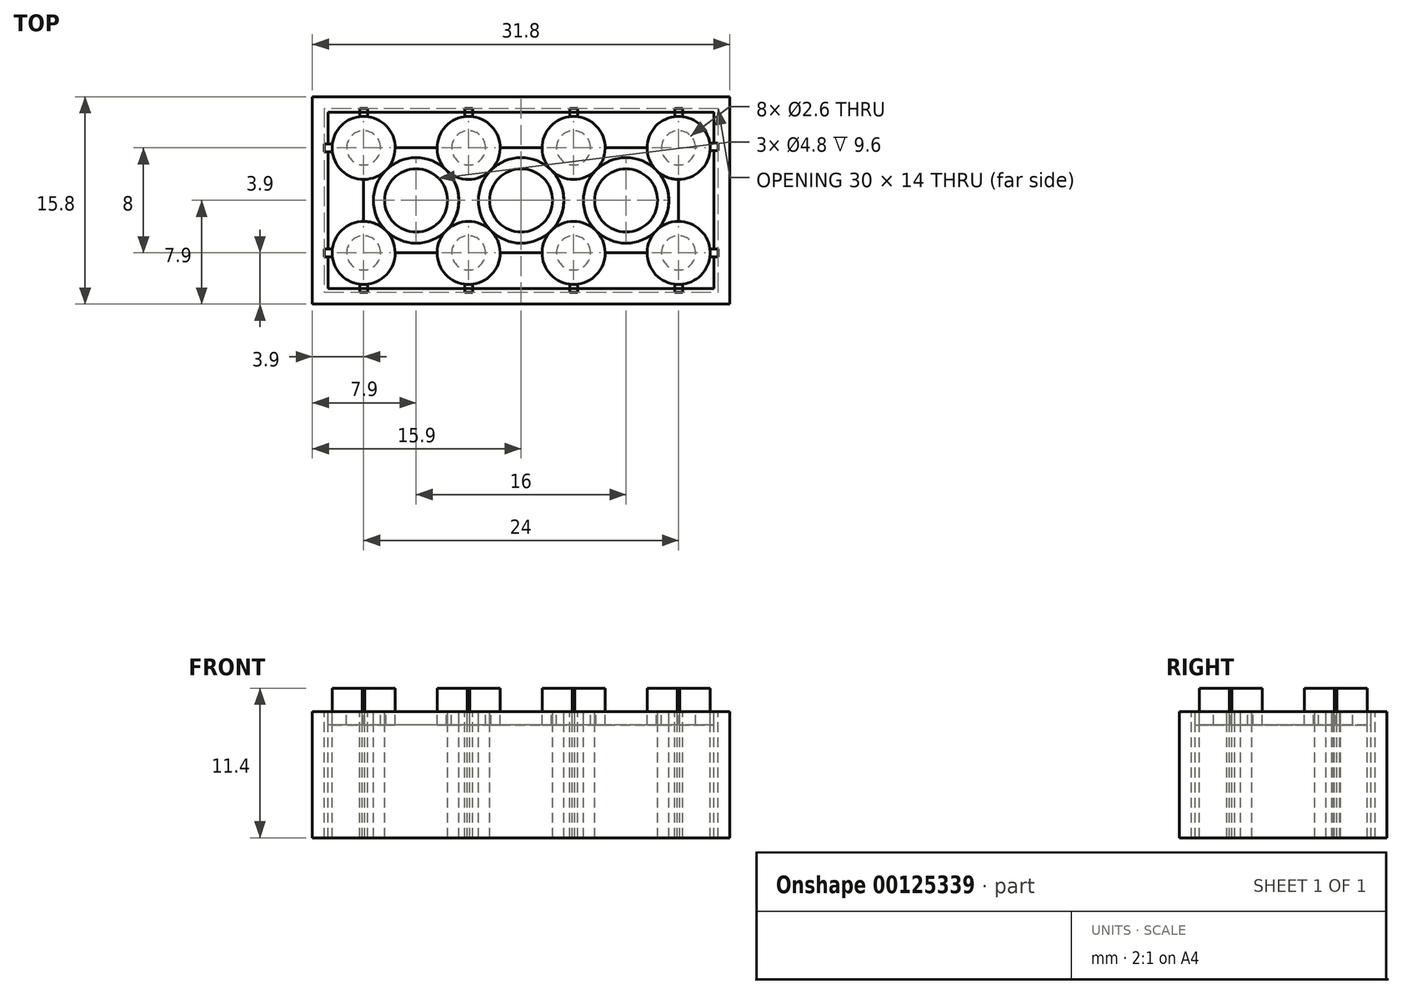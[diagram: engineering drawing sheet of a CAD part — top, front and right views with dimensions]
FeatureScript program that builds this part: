
annotation { "Feature Type Name" : "Feature", "Feature Type Description" : "" }
export const myFeature = defineFeature(function(context is Context, id is Id, definition is map)
    precondition{}
    {
        {
            var Q0;
            Q0=qCreatedBy(makeId("Top.planeOp"),FACE);
            var sketch = newSketch(context, id + "F0", { "sketchPlane" : qUnion([Q0])});
            skLineSegment(sketch, "E0.bottom", {"start": v(-15.9, -7.9) * mm, "end": v(15.9, -7.9) * mm});
            skLineSegment(sketch, "E0.top", {"start": v(-15.9, 7.9) * mm, "end": v(15.9, 7.9) * mm});
            skLineSegment(sketch, "E0.left", {"start": v(-15.9, -7.9) * mm, "end": v(-15.9, 7.9) * mm});
            skLineSegment(sketch, "E0.right", {"start": v(15.9, -7.9) * mm, "end": v(15.9, 7.9) * mm});
            skPoint(sketch, "E0.middle", {"position": v(0, 0) * mm});
            skCircle(sketch, "E1", {"center": v(0, 0) * mm, "radius": 3.26 * mm});
            skCircle(sketch, "E2", {"center": v(0, 0) * mm, "radius": 2.4 * mm});
            skLineSegment(sketch, "E3.bottom", {"start": v(14.7, -6.7) * mm, "end": v(-14.7, -6.7) * mm});
            skLineSegment(sketch, "E3.top", {"start": v(14.7, 6.7) * mm, "end": v(-14.7, 6.7) * mm});
            skLineSegment(sketch, "E3.left", {"start": v(14.7, -6.7) * mm, "end": v(14.7, 6.7) * mm});
            skLineSegment(sketch, "E3.right", {"start": v(-14.7, -6.7) * mm, "end": v(-14.7, 6.7) * mm});
            skPoint(sketch, "E4.endSnap0", {"position": v(-14.7, 0) * mm});
            skPoint(sketch, "E5.endSnap0", {"position": v(14.7, 0) * mm});
            skCircle(sketch, "E6", {"center": v(8, 0) * mm, "radius": 3.26 * mm});
            skCircle(sketch, "E7", {"center": v(8, 0) * mm, "radius": 2.4 * mm});
            skCircle(sketch, "E8", {"center": v(-8, 0) * mm, "radius": 3.26 * mm});
            skCircle(sketch, "E9", {"center": v(-8, 0) * mm, "radius": 2.4 * mm});
            skLineSegment(sketch, "E10", {"start": v(-14.7, 0) * mm, "end": v(14.7, 0) * mm});
            skLineSegment(sketch, "E11.bottom", {"start": v(-4, 4) * mm, "end": v(4, 4) * mm});
            skLineSegment(sketch, "E11.top", {"start": v(-4, -4) * mm, "end": v(4, -4) * mm});
            skLineSegment(sketch, "E11.left", {"start": v(-4, 4) * mm, "end": v(-4, -4) * mm});
            skLineSegment(sketch, "E11.right", {"start": v(4, 4) * mm, "end": v(4, -4) * mm});
            skCircle(sketch, "E12", {"center": v(-4, 4) * mm, "radius": 2.4 * mm});
            skCircle(sketch, "E13", {"center": v(4, 4) * mm, "radius": 2.4 * mm});
            skCircle(sketch, "E14", {"center": v(4, -4) * mm, "radius": 2.4 * mm});
            skCircle(sketch, "E15", {"center": v(-4, -4) * mm, "radius": 2.4 * mm});
            skCircle(sketch, "E16", {"center": v(-4, 4) * mm, "radius": 1.3 * mm});
            skCircle(sketch, "E17", {"center": v(4, 4) * mm, "radius": 1.3 * mm});
            skCircle(sketch, "E18", {"center": v(-4, -4) * mm, "radius": 1.3 * mm});
            skCircle(sketch, "E19", {"center": v(4, -4) * mm, "radius": 1.3 * mm});
            skLineSegment(sketch, "E20", {"start": v(-8, 0) * mm, "end": v(0, 0) * mm});
            skLineSegment(sketch, "E21", {"start": v(0, 0) * mm, "end": v(8, 0) * mm});
            skLineSegment(sketch, "E22.bottom", {"start": v(-4, 4) * mm, "end": v(-12, 4) * mm});
            skLineSegment(sketch, "E22.top", {"start": v(-4, -4) * mm, "end": v(-12, -4) * mm});
            skLineSegment(sketch, "E22.right", {"start": v(-12, 4) * mm, "end": v(-12, -4) * mm});
            skLineSegment(sketch, "E23.bottom", {"start": v(4, 4) * mm, "end": v(12, 4) * mm});
            skLineSegment(sketch, "E23.top", {"start": v(4, -4) * mm, "end": v(12, -4) * mm});
            skLineSegment(sketch, "E23.right", {"start": v(12, 4) * mm, "end": v(12, -4) * mm});
            skCircle(sketch, "E24", {"center": v(-12, 4) * mm, "radius": 2.4 * mm});
            skCircle(sketch, "E25", {"center": v(-12, -4) * mm, "radius": 2.4 * mm});
            skCircle(sketch, "E26", {"center": v(12, -4) * mm, "radius": 2.4 * mm});
            skCircle(sketch, "E27", {"center": v(12, 4) * mm, "radius": 2.4 * mm});
            skCircle(sketch, "E28", {"center": v(-12, 4) * mm, "radius": 1.3 * mm});
            skCircle(sketch, "E29", {"center": v(-12, -4) * mm, "radius": 1.3 * mm});
            skCircle(sketch, "E30", {"center": v(12, -4) * mm, "radius": 1.3 * mm});
            skCircle(sketch, "E31", {"center": v(12, 4) * mm, "radius": 1.3 * mm});
            skLineSegment(sketch, "E32.bottom", {"start": v(-14.4, 4.3) * mm, "end": v(-15, 4.3) * mm});
            skLineSegment(sketch, "E32.top", {"start": v(-14.4, 3.7) * mm, "end": v(-15, 3.7) * mm});
            skLineSegment(sketch, "E32.left", {"start": v(-14.4, 4.3) * mm, "end": v(-14.4, 3.7) * mm});
            skLineSegment(sketch, "E32.right", {"start": v(-15, 4.3) * mm, "end": v(-15, 3.7) * mm});
            skPoint(sketch, "E32.middle", {"position": v(-14.7, 4) * mm});
            skLineSegment(sketch, "E33.bottom", {"start": v(-14.4, -3.7) * mm, "end": v(-15, -3.7) * mm});
            skLineSegment(sketch, "E33.top", {"start": v(-14.4, -4.3) * mm, "end": v(-15, -4.3) * mm});
            skLineSegment(sketch, "E33.left", {"start": v(-14.4, -3.7) * mm, "end": v(-14.4, -4.3) * mm});
            skLineSegment(sketch, "E33.right", {"start": v(-15, -3.7) * mm, "end": v(-15, -4.3) * mm});
            skPoint(sketch, "E33.middle", {"position": v(-14.7, -4) * mm});
            skLineSegment(sketch, "E34.bottom", {"start": v(-3.7, 6.4) * mm, "end": v(-4.3, 6.4) * mm});
            skLineSegment(sketch, "E34.top", {"start": v(-3.7, 7) * mm, "end": v(-4.3, 7) * mm});
            skLineSegment(sketch, "E34.left", {"start": v(-3.7, 6.4) * mm, "end": v(-3.7, 7) * mm});
            skLineSegment(sketch, "E34.right", {"start": v(-4.3, 6.4) * mm, "end": v(-4.3, 7) * mm});
            skPoint(sketch, "E34.middle", {"position": v(-4, 6.7) * mm});
            skLineSegment(sketch, "E35.bottom", {"start": v(4.3, 6.4) * mm, "end": v(3.7, 6.4) * mm});
            skLineSegment(sketch, "E35.top", {"start": v(4.3, 7) * mm, "end": v(3.7, 7) * mm});
            skLineSegment(sketch, "E35.left", {"start": v(4.3, 6.4) * mm, "end": v(4.3, 7) * mm});
            skLineSegment(sketch, "E35.right", {"start": v(3.7, 6.4) * mm, "end": v(3.7, 7) * mm});
            skPoint(sketch, "E35.middle", {"position": v(4, 6.7) * mm});
            skLineSegment(sketch, "E36.bottom", {"start": v(12.3, 6.4) * mm, "end": v(11.7, 6.4) * mm});
            skLineSegment(sketch, "E36.top", {"start": v(12.3, 7) * mm, "end": v(11.7, 7) * mm});
            skLineSegment(sketch, "E36.left", {"start": v(12.3, 6.4) * mm, "end": v(12.3, 7) * mm});
            skLineSegment(sketch, "E36.right", {"start": v(11.7, 6.4) * mm, "end": v(11.7, 7) * mm});
            skPoint(sketch, "E36.middle", {"position": v(12, 6.7) * mm});
            skLineSegment(sketch, "E37.bottom", {"start": v(-11.7, 6.4) * mm, "end": v(-12.3, 6.4) * mm});
            skLineSegment(sketch, "E37.top", {"start": v(-11.7, 7) * mm, "end": v(-12.3, 7) * mm});
            skLineSegment(sketch, "E37.left", {"start": v(-11.7, 6.4) * mm, "end": v(-11.7, 7) * mm});
            skLineSegment(sketch, "E37.right", {"start": v(-12.3, 6.4) * mm, "end": v(-12.3, 7) * mm});
            skPoint(sketch, "E37.middle", {"position": v(-12, 6.7) * mm});
            skLineSegment(sketch, "E38.bottom", {"start": v(-11.7, -6.4) * mm, "end": v(-12.3, -6.4) * mm});
            skLineSegment(sketch, "E38.top", {"start": v(-11.7, -7) * mm, "end": v(-12.3, -7) * mm});
            skLineSegment(sketch, "E38.left", {"start": v(-11.7, -6.4) * mm, "end": v(-11.7, -7) * mm});
            skLineSegment(sketch, "E38.right", {"start": v(-12.3, -6.4) * mm, "end": v(-12.3, -7) * mm});
            skPoint(sketch, "E38.middle", {"position": v(-12, -6.7) * mm});
            skLineSegment(sketch, "E39.bottom", {"start": v(-3.7, -6.4) * mm, "end": v(-4.3, -6.4) * mm});
            skLineSegment(sketch, "E39.top", {"start": v(-3.7, -7) * mm, "end": v(-4.3, -7) * mm});
            skLineSegment(sketch, "E39.left", {"start": v(-3.7, -6.4) * mm, "end": v(-3.7, -7) * mm});
            skLineSegment(sketch, "E39.right", {"start": v(-4.3, -6.4) * mm, "end": v(-4.3, -7) * mm});
            skPoint(sketch, "E39.middle", {"position": v(-4, -6.7) * mm});
            skLineSegment(sketch, "E40.bottom", {"start": v(4.3, -6.4) * mm, "end": v(3.7, -6.4) * mm});
            skLineSegment(sketch, "E40.top", {"start": v(4.3, -7) * mm, "end": v(3.7, -7) * mm});
            skLineSegment(sketch, "E40.left", {"start": v(4.3, -6.4) * mm, "end": v(4.3, -7) * mm});
            skLineSegment(sketch, "E40.right", {"start": v(3.7, -6.4) * mm, "end": v(3.7, -7) * mm});
            skPoint(sketch, "E40.middle", {"position": v(4, -6.7) * mm});
            skLineSegment(sketch, "E41.bottom", {"start": v(12.3, -6.4) * mm, "end": v(11.7, -6.4) * mm});
            skLineSegment(sketch, "E41.top", {"start": v(12.3, -7) * mm, "end": v(11.7, -7) * mm});
            skLineSegment(sketch, "E41.left", {"start": v(12.3, -6.4) * mm, "end": v(12.3, -7) * mm});
            skLineSegment(sketch, "E41.right", {"start": v(11.7, -6.4) * mm, "end": v(11.7, -7) * mm});
            skPoint(sketch, "E41.middle", {"position": v(12, -6.7) * mm});
            skLineSegment(sketch, "E42.bottom", {"start": v(14.4, -3.7) * mm, "end": v(15, -3.7) * mm});
            skLineSegment(sketch, "E42.top", {"start": v(14.4, -4.3) * mm, "end": v(15, -4.3) * mm});
            skLineSegment(sketch, "E42.left", {"start": v(14.4, -3.7) * mm, "end": v(14.4, -4.3) * mm});
            skLineSegment(sketch, "E42.right", {"start": v(15, -3.7) * mm, "end": v(15, -4.3) * mm});
            skPoint(sketch, "E42.middle", {"position": v(14.7, -4) * mm});
            skLineSegment(sketch, "E43.bottom", {"start": v(14.4, 4.38) * mm, "end": v(15, 4.38) * mm});
            skLineSegment(sketch, "E43.top", {"start": v(14.4, 3.78) * mm, "end": v(15, 3.78) * mm});
            skLineSegment(sketch, "E43.left", {"start": v(14.4, 4.38) * mm, "end": v(14.4, 3.78) * mm});
            skLineSegment(sketch, "E43.right", {"start": v(15, 4.38) * mm, "end": v(15, 3.78) * mm});
            skPoint(sketch, "E43.middle", {"position": v(14.7, 4.08) * mm});
            skSolve(sketch);
        }
        {
            var Q0;
            Q0=makeQuery(id+"F0.imprint","IMPRINT",FACE,{"disambiguationData":[TD([[makeQuery(id+"F0.imprint","IMPRINT",EDGE,{"derivedFrom":sQuery(id+"F0.wireOp",EDGE,"E0.bottom")}),1.0]])]});
            extrude(context, id + "F1", {"entities" : qUnion([Q0]), "oppositeDirection" : true, "depth" : 9.6 * mm});
        }
        {
            var Q0;
            Q0=sQuery(id+"F0.wireOp",EDGE,"E25");
            var Q1;
            Q1=sQuery(id+"F0.wireOp",EDGE,"E29");
            var Q2;
            Q2=sQuery(id+"F0.wireOp",EDGE,"E15");
            var Q3;
            Q3=sQuery(id+"F0.wireOp",EDGE,"E18");
            var Q4;
            Q4=sQuery(id+"F0.wireOp",EDGE,"E14");
            var Q5;
            Q5=sQuery(id+"F0.wireOp",EDGE,"E19");
            var Q6;
            Q6=sQuery(id+"F0.wireOp",EDGE,"E26");
            var Q7;
            Q7=sQuery(id+"F0.wireOp",EDGE,"E30");
            var Q8;
            Q8=sQuery(id+"F0.wireOp",EDGE,"E27");
            var Q9;
            Q9=sQuery(id+"F0.wireOp",EDGE,"E31");
            var Q10;
            Q10=sQuery(id+"F0.wireOp",EDGE,"E13");
            var Q11;
            Q11=sQuery(id+"F0.wireOp",EDGE,"E17");
            var Q12;
            Q12=sQuery(id+"F0.wireOp",EDGE,"E12");
            var Q13;
            Q13=sQuery(id+"F0.wireOp",EDGE,"E16");
            var Q14;
            Q14=sQuery(id+"F0.wireOp",EDGE,"E24");
            var Q15;
            Q15=sQuery(id+"F0.wireOp",EDGE,"E28");
            extrude(context, id + "F2", {"bodyType" : ToolBodyType.SURFACE, "surfaceEntities" : qUnion([Q0, Q1, Q2, Q3, Q4, Q5, Q6, Q7, Q8, Q9, Q10, Q11, Q12, Q13, Q14, Q15]), "depth" : 1.8 * mm});
        }
        {
            var Q0;
            {var subQ0=sQuery(id+"F0.wireOp",EDGE,"E24");var subQ1=sQuery(id+"F0.wireOp",EDGE,"E22.bottom");var subQ2=makeQuery(id+"F0.imprint","INTERSECT",VERTEX,{"derivedFrom":[subQ1,subQ0]});Q0=makeQuery(id+"F0.imprint","IMPRINT",FACE,{"disambiguationData":[TD([[makeQuery(id+"F0.imprint","IMPRINT",EDGE,{"disambiguationData":[TD([[subQ2,-1.0]])],"derivedFrom":subQ1}),-1.0]])]});}
            var Q1;
            {var subQ0=sQuery(id+"F0.wireOp",EDGE,"E24");var subQ2=sQuery(id+"F0.wireOp",EDGE,"E22.bottom");var subQ3=makeQuery(id+"F0.imprint","INTERSECT",VERTEX,{"derivedFrom":[subQ2,subQ0]});Q1=makeQuery(id+"F0.imprint","IMPRINT",FACE,{"disambiguationData":[TD([[makeQuery(id+"F0.imprint","IMPRINT",EDGE,{"disambiguationData":[TD([[subQ3,-1.0]])],"derivedFrom":subQ2}),1.0]])]});}
            var Q2;
            {var subQ0=sQuery(id+"F0.wireOp",EDGE,"E16");var subQ1=sQuery(id+"F0.wireOp",EDGE,"E11.bottom");var subQ2=makeQuery(id+"F0.imprint","INTERSECT",VERTEX,{"derivedFrom":[subQ1,subQ0]});Q2=makeQuery(id+"F0.imprint","IMPRINT",FACE,{"disambiguationData":[TD([[makeQuery(id+"F0.imprint","IMPRINT",EDGE,{"disambiguationData":[TD([[subQ2,-1.0]])],"derivedFrom":subQ1}),1.0]])]});}
            var Q3;
            {var subQ1=sQuery(id+"F0.wireOp",EDGE,"E12");var subQ7=makeQuery(id+"F0.imprint","INTERSECT",VERTEX,{"derivedFrom":[sQuery(id+"F0.wireOp",EDGE,"E8"),subQ1]});Q3=makeQuery(id+"F0.imprint","IMPRINT",FACE,{"disambiguationData":[TD([[makeQuery(id+"F0.imprint","IMPRINT",EDGE,{"disambiguationData":[TD([[subQ7,1.0]])],"derivedFrom":subQ1}),1.0]])]});}
            var Q4;
            {var subQ2=sQuery(id+"F0.wireOp",EDGE,"E11.bottom");var subQ6=sQuery(id+"F0.wireOp",EDGE,"E16");var subQ7=makeQuery(id+"F0.imprint","INTERSECT",VERTEX,{"derivedFrom":[subQ2,subQ6]});Q4=makeQuery(id+"F0.imprint","IMPRINT",FACE,{"disambiguationData":[TD([[makeQuery(id+"F0.imprint","IMPRINT",EDGE,{"disambiguationData":[TD([[subQ7,-1.0]])],"derivedFrom":subQ2}),-1.0]])]});}
            var Q5;
            {var subQ0=sQuery(id+"F0.wireOp",EDGE,"E13");var subQ1=sQuery(id+"F0.wireOp",EDGE,"E11.bottom");var subQ2=makeQuery(id+"F0.imprint","INTERSECT",VERTEX,{"derivedFrom":[subQ1,subQ0]});Q5=makeQuery(id+"F0.imprint","IMPRINT",FACE,{"disambiguationData":[TD([[makeQuery(id+"F0.imprint","IMPRINT",EDGE,{"disambiguationData":[TD([[subQ2,-1.0]])],"derivedFrom":subQ1}),1.0]])]});}
            var Q6;
            {var subQ1=sQuery(id+"F0.wireOp",EDGE,"E11.bottom");var subQ5=sQuery(id+"F0.wireOp",EDGE,"E13");var subQ7=makeQuery(id+"F0.imprint","INTERSECT",VERTEX,{"derivedFrom":[subQ1,subQ5]});Q6=makeQuery(id+"F0.imprint","IMPRINT",FACE,{"disambiguationData":[TD([[makeQuery(id+"F0.imprint","IMPRINT",EDGE,{"disambiguationData":[TD([[subQ7,-1.0]])],"derivedFrom":subQ1}),-1.0]])]});}
            var Q7;
            {var subQ1=sQuery(id+"F0.wireOp",EDGE,"E13");var subQ5=makeQuery(id+"F0.imprint","INTERSECT",VERTEX,{"derivedFrom":[sQuery(id+"F0.wireOp",EDGE,"E6"),subQ1]});Q7=makeQuery(id+"F0.imprint","IMPRINT",FACE,{"disambiguationData":[TD([[makeQuery(id+"F0.imprint","IMPRINT",EDGE,{"disambiguationData":[TD([[subQ5,1.0]])],"derivedFrom":subQ1}),1.0]])]});}
            var Q8;
            {var subQ0=sQuery(id+"F0.wireOp",EDGE,"E27");var subQ4=sQuery(id+"F0.wireOp",EDGE,"E23.bottom");var subQ5=makeQuery(id+"F0.imprint","INTERSECT",VERTEX,{"derivedFrom":[subQ4,subQ0]});Q8=makeQuery(id+"F0.imprint","IMPRINT",FACE,{"disambiguationData":[TD([[makeQuery(id+"F0.imprint","IMPRINT",EDGE,{"disambiguationData":[TD([[subQ5,-1.0]])],"derivedFrom":subQ4}),-1.0]])]});}
            var Q9;
            {var subQ0=sQuery(id+"F0.wireOp",EDGE,"E27");var subQ1=sQuery(id+"F0.wireOp",EDGE,"E23.bottom");var subQ2=makeQuery(id+"F0.imprint","INTERSECT",VERTEX,{"derivedFrom":[subQ1,subQ0]});Q9=makeQuery(id+"F0.imprint","IMPRINT",FACE,{"disambiguationData":[TD([[makeQuery(id+"F0.imprint","IMPRINT",EDGE,{"disambiguationData":[TD([[subQ2,-1.0]])],"derivedFrom":subQ1}),1.0]])]});}
            var Q10;
            {var subQ0=sQuery(id+"F0.wireOp",EDGE,"E26");var subQ2=sQuery(id+"F0.wireOp",EDGE,"E23.top");var subQ3=makeQuery(id+"F0.imprint","INTERSECT",VERTEX,{"derivedFrom":[subQ2,subQ0]});Q10=makeQuery(id+"F0.imprint","IMPRINT",FACE,{"disambiguationData":[TD([[makeQuery(id+"F0.imprint","IMPRINT",EDGE,{"disambiguationData":[TD([[subQ3,-1.0]])],"derivedFrom":subQ2}),1.0]])]});}
            var Q11;
            {var subQ0=sQuery(id+"F0.wireOp",EDGE,"E26");var subQ1=sQuery(id+"F0.wireOp",EDGE,"E23.top");var subQ2=makeQuery(id+"F0.imprint","INTERSECT",VERTEX,{"derivedFrom":[subQ1,subQ0]});Q11=makeQuery(id+"F0.imprint","IMPRINT",FACE,{"disambiguationData":[TD([[makeQuery(id+"F0.imprint","IMPRINT",EDGE,{"disambiguationData":[TD([[subQ2,-1.0]])],"derivedFrom":subQ1}),-1.0]])]});}
            var Q12;
            {var subQ1=sQuery(id+"F0.wireOp",EDGE,"E11.top");var subQ5=sQuery(id+"F0.wireOp",EDGE,"E14");var subQ7=makeQuery(id+"F0.imprint","INTERSECT",VERTEX,{"derivedFrom":[subQ1,subQ5]});Q12=makeQuery(id+"F0.imprint","IMPRINT",FACE,{"disambiguationData":[TD([[makeQuery(id+"F0.imprint","IMPRINT",EDGE,{"disambiguationData":[TD([[subQ7,-1.0]])],"derivedFrom":subQ1}),1.0]])]});}
            var Q13;
            {var subQ5=sQuery(id+"F0.wireOp",EDGE,"E14");var subQ7=makeQuery(id+"F0.imprint","INTERSECT",VERTEX,{"derivedFrom":[sQuery(id+"F0.wireOp",EDGE,"E6"),subQ5]});Q13=makeQuery(id+"F0.imprint","IMPRINT",FACE,{"disambiguationData":[TD([[makeQuery(id+"F0.imprint","IMPRINT",EDGE,{"disambiguationData":[TD([[subQ7,1.0]])],"derivedFrom":subQ5}),1.0]])]});}
            var Q14;
            {var subQ0=sQuery(id+"F0.wireOp",EDGE,"E18");var subQ1=sQuery(id+"F0.wireOp",EDGE,"E11.top");var subQ2=makeQuery(id+"F0.imprint","INTERSECT",VERTEX,{"derivedFrom":[subQ1,subQ0]});Q14=makeQuery(id+"F0.imprint","IMPRINT",FACE,{"disambiguationData":[TD([[makeQuery(id+"F0.imprint","IMPRINT",EDGE,{"disambiguationData":[TD([[subQ2,-1.0]])],"derivedFrom":subQ1}),1.0]])]});}
            var Q15;
            {var subQ1=sQuery(id+"F0.wireOp",EDGE,"E15");var subQ7=makeQuery(id+"F0.imprint","INTERSECT",VERTEX,{"derivedFrom":[sQuery(id+"F0.wireOp",EDGE,"E8"),subQ1]});Q15=makeQuery(id+"F0.imprint","IMPRINT",FACE,{"disambiguationData":[TD([[makeQuery(id+"F0.imprint","IMPRINT",EDGE,{"disambiguationData":[TD([[subQ7,1.0]])],"derivedFrom":subQ1}),1.0]])]});}
            var Q16;
            {var subQ0=sQuery(id+"F0.wireOp",EDGE,"E18");var subQ1=sQuery(id+"F0.wireOp",EDGE,"E11.top");var subQ2=makeQuery(id+"F0.imprint","INTERSECT",VERTEX,{"derivedFrom":[subQ1,subQ0]});Q16=makeQuery(id+"F0.imprint","IMPRINT",FACE,{"disambiguationData":[TD([[makeQuery(id+"F0.imprint","IMPRINT",EDGE,{"disambiguationData":[TD([[subQ2,-1.0]])],"derivedFrom":subQ1}),-1.0]])]});}
            var Q17;
            {var subQ0=sQuery(id+"F0.wireOp",EDGE,"E25");var subQ1=sQuery(id+"F0.wireOp",EDGE,"E22.top");var subQ2=makeQuery(id+"F0.imprint","INTERSECT",VERTEX,{"derivedFrom":[subQ1,subQ0]});Q17=makeQuery(id+"F0.imprint","IMPRINT",FACE,{"disambiguationData":[TD([[makeQuery(id+"F0.imprint","IMPRINT",EDGE,{"disambiguationData":[TD([[subQ2,-1.0]])],"derivedFrom":subQ1}),1.0]])]});}
            var Q18;
            {var subQ0=sQuery(id+"F0.wireOp",EDGE,"E25");var subQ2=sQuery(id+"F0.wireOp",EDGE,"E22.top");var subQ3=makeQuery(id+"F0.imprint","INTERSECT",VERTEX,{"derivedFrom":[subQ2,subQ0]});Q18=makeQuery(id+"F0.imprint","IMPRINT",FACE,{"disambiguationData":[TD([[makeQuery(id+"F0.imprint","IMPRINT",EDGE,{"disambiguationData":[TD([[subQ3,-1.0]])],"derivedFrom":subQ2}),-1.0]])]});}
            var Q19;
            {var subQ0=sQuery(id+"F0.wireOp",EDGE,"E14");var subQ1=sQuery(id+"F0.wireOp",EDGE,"E11.top");var subQ2=makeQuery(id+"F0.imprint","INTERSECT",VERTEX,{"derivedFrom":[subQ1,subQ0]});Q19=makeQuery(id+"F0.imprint","IMPRINT",FACE,{"disambiguationData":[TD([[makeQuery(id+"F0.imprint","IMPRINT",EDGE,{"disambiguationData":[TD([[subQ2,-1.0]])],"derivedFrom":subQ1}),-1.0]])]});}
            var Q20;
            {var subQ0=sQuery(id+"F0.wireOp",EDGE,"E22.right");var subQ1=sQuery(id+"F0.wireOp",EDGE,"E22.bottom");var subQ2=makeQuery(id+"F0.imprint","INTERSECT",VERTEX,{"derivedFrom":[subQ1,subQ0]});Q20=makeQuery(id+"F0.imprint","IMPRINT",FACE,{"disambiguationData":[TD([[makeQuery(id+"F0.imprint","IMPRINT",EDGE,{"disambiguationData":[TD([[subQ2,1.0]])],"derivedFrom":subQ1}),-1.0]])]});}
            var Q21;
            {var subQ0=sQuery(id+"F0.wireOp",EDGE,"E22.right");var subQ1=sQuery(id+"F0.wireOp",EDGE,"E22.bottom");var subQ2=makeQuery(id+"F0.imprint","INTERSECT",VERTEX,{"derivedFrom":[subQ1,subQ0]});Q21=makeQuery(id+"F0.imprint","IMPRINT",FACE,{"disambiguationData":[TD([[makeQuery(id+"F0.imprint","IMPRINT",EDGE,{"disambiguationData":[TD([[subQ2,1.0]])],"derivedFrom":subQ1}),1.0]])]});}
            var Q22;
            {var subQ1=sQuery(id+"F0.wireOp",EDGE,"E11.bottom");var subQ3=sQuery(id+"F0.wireOp",EDGE,"E16");var subQ4=makeQuery(id+"F0.imprint","INTERSECT",VERTEX,{"derivedFrom":[subQ1,subQ3]});Q22=makeQuery(id+"F0.imprint","IMPRINT",FACE,{"disambiguationData":[TD([[makeQuery(id+"F0.imprint","IMPRINT",EDGE,{"disambiguationData":[TD([[subQ4,-1.0]])],"derivedFrom":subQ3}),1.0]])]});}
            var Q23;
            {var subQ0=sQuery(id+"F0.wireOp",EDGE,"E22.bottom");var subQ1=sQuery(id+"F0.wireOp",EDGE,"E16");var subQ2=makeQuery(id+"F0.imprint","INTERSECT",VERTEX,{"derivedFrom":[subQ1,subQ0]});Q23=makeQuery(id+"F0.imprint","IMPRINT",FACE,{"disambiguationData":[TD([[makeQuery(id+"F0.imprint","IMPRINT",EDGE,{"disambiguationData":[TD([[subQ2,-1.0]])],"derivedFrom":subQ1}),1.0]])]});}
            var Q24;
            {var subQ1=sQuery(id+"F0.wireOp",EDGE,"E11.bottom");var subQ3=sQuery(id+"F0.wireOp",EDGE,"E16");var subQ4=makeQuery(id+"F0.imprint","INTERSECT",VERTEX,{"derivedFrom":[subQ1,subQ3]});Q24=makeQuery(id+"F0.imprint","IMPRINT",FACE,{"disambiguationData":[TD([[makeQuery(id+"F0.imprint","IMPRINT",EDGE,{"disambiguationData":[TD([[subQ4,1.0]])],"derivedFrom":subQ3}),1.0]])]});}
            var Q25;
            {var subQ1=sQuery(id+"F0.wireOp",EDGE,"E11.bottom");var subQ3=sQuery(id+"F0.wireOp",EDGE,"E17");var subQ4=makeQuery(id+"F0.imprint","INTERSECT",VERTEX,{"derivedFrom":[subQ1,subQ3]});Q25=makeQuery(id+"F0.imprint","IMPRINT",FACE,{"disambiguationData":[TD([[makeQuery(id+"F0.imprint","IMPRINT",EDGE,{"disambiguationData":[TD([[subQ4,1.0]])],"derivedFrom":subQ3}),1.0]])]});}
            var Q26;
            {var subQ1=sQuery(id+"F0.wireOp",EDGE,"E11.bottom");var subQ3=sQuery(id+"F0.wireOp",EDGE,"E17");var subQ4=makeQuery(id+"F0.imprint","INTERSECT",VERTEX,{"derivedFrom":[subQ1,subQ3]});Q26=makeQuery(id+"F0.imprint","IMPRINT",FACE,{"disambiguationData":[TD([[makeQuery(id+"F0.imprint","IMPRINT",EDGE,{"disambiguationData":[TD([[subQ4,-1.0]])],"derivedFrom":subQ3}),1.0]])]});}
            var Q27;
            {var subQ0=sQuery(id+"F0.wireOp",EDGE,"E23.bottom");var subQ1=sQuery(id+"F0.wireOp",EDGE,"E17");var subQ2=makeQuery(id+"F0.imprint","INTERSECT",VERTEX,{"derivedFrom":[subQ1,subQ0]});Q27=makeQuery(id+"F0.imprint","IMPRINT",FACE,{"disambiguationData":[TD([[makeQuery(id+"F0.imprint","IMPRINT",EDGE,{"disambiguationData":[TD([[subQ2,1.0]])],"derivedFrom":subQ1}),1.0]])]});}
            var Q28;
            {var subQ0=sQuery(id+"F0.wireOp",EDGE,"E23.right");var subQ1=sQuery(id+"F0.wireOp",EDGE,"E23.bottom");var subQ2=makeQuery(id+"F0.imprint","INTERSECT",VERTEX,{"derivedFrom":[subQ1,subQ0]});Q28=makeQuery(id+"F0.imprint","IMPRINT",FACE,{"disambiguationData":[TD([[makeQuery(id+"F0.imprint","IMPRINT",EDGE,{"disambiguationData":[TD([[subQ2,1.0]])],"derivedFrom":subQ1}),1.0]])]});}
            var Q29;
            {var subQ0=sQuery(id+"F0.wireOp",EDGE,"E23.right");var subQ1=sQuery(id+"F0.wireOp",EDGE,"E23.bottom");var subQ2=makeQuery(id+"F0.imprint","INTERSECT",VERTEX,{"derivedFrom":[subQ1,subQ0]});Q29=makeQuery(id+"F0.imprint","IMPRINT",FACE,{"disambiguationData":[TD([[makeQuery(id+"F0.imprint","IMPRINT",EDGE,{"disambiguationData":[TD([[subQ2,1.0]])],"derivedFrom":subQ1}),-1.0]])]});}
            var Q30;
            {var subQ0=sQuery(id+"F0.wireOp",EDGE,"E23.right");var subQ1=sQuery(id+"F0.wireOp",EDGE,"E23.top");var subQ2=makeQuery(id+"F0.imprint","INTERSECT",VERTEX,{"derivedFrom":[subQ1,subQ0]});Q30=makeQuery(id+"F0.imprint","IMPRINT",FACE,{"disambiguationData":[TD([[makeQuery(id+"F0.imprint","IMPRINT",EDGE,{"disambiguationData":[TD([[subQ2,1.0]])],"derivedFrom":subQ1}),1.0]])]});}
            var Q31;
            {var subQ0=sQuery(id+"F0.wireOp",EDGE,"E23.right");var subQ1=sQuery(id+"F0.wireOp",EDGE,"E23.top");var subQ2=makeQuery(id+"F0.imprint","INTERSECT",VERTEX,{"derivedFrom":[subQ1,subQ0]});Q31=makeQuery(id+"F0.imprint","IMPRINT",FACE,{"disambiguationData":[TD([[makeQuery(id+"F0.imprint","IMPRINT",EDGE,{"disambiguationData":[TD([[subQ2,1.0]])],"derivedFrom":subQ1}),-1.0]])]});}
            var Q32;
            {var subQ0=sQuery(id+"F0.wireOp",EDGE,"E11.right");var subQ1=sQuery(id+"F0.wireOp",EDGE,"E19");var subQ2=makeQuery(id+"F0.imprint","INTERSECT",VERTEX,{"derivedFrom":[subQ1,subQ0]});Q32=makeQuery(id+"F0.imprint","IMPRINT",FACE,{"disambiguationData":[TD([[makeQuery(id+"F0.imprint","IMPRINT",EDGE,{"disambiguationData":[TD([[subQ2,1.0]])],"derivedFrom":subQ1}),1.0]])]});}
            var Q33;
            {var subQ1=sQuery(id+"F0.wireOp",EDGE,"E11.top");var subQ3=sQuery(id+"F0.wireOp",EDGE,"E19");var subQ4=makeQuery(id+"F0.imprint","INTERSECT",VERTEX,{"derivedFrom":[subQ1,subQ3]});Q33=makeQuery(id+"F0.imprint","IMPRINT",FACE,{"disambiguationData":[TD([[makeQuery(id+"F0.imprint","IMPRINT",EDGE,{"disambiguationData":[TD([[subQ4,1.0]])],"derivedFrom":subQ3}),1.0]])]});}
            var Q34;
            {var subQ1=sQuery(id+"F0.wireOp",EDGE,"E11.top");var subQ3=sQuery(id+"F0.wireOp",EDGE,"E19");var subQ4=makeQuery(id+"F0.imprint","INTERSECT",VERTEX,{"derivedFrom":[subQ1,subQ3]});Q34=makeQuery(id+"F0.imprint","IMPRINT",FACE,{"disambiguationData":[TD([[makeQuery(id+"F0.imprint","IMPRINT",EDGE,{"disambiguationData":[TD([[subQ4,-1.0]])],"derivedFrom":subQ3}),1.0]])]});}
            var Q35;
            {var subQ1=sQuery(id+"F0.wireOp",EDGE,"E11.top");var subQ3=sQuery(id+"F0.wireOp",EDGE,"E18");var subQ4=makeQuery(id+"F0.imprint","INTERSECT",VERTEX,{"derivedFrom":[subQ1,subQ3]});Q35=makeQuery(id+"F0.imprint","IMPRINT",FACE,{"disambiguationData":[TD([[makeQuery(id+"F0.imprint","IMPRINT",EDGE,{"disambiguationData":[TD([[subQ4,-1.0]])],"derivedFrom":subQ3}),1.0]])]});}
            var Q36;
            {var subQ0=sQuery(id+"F0.wireOp",EDGE,"E11.left");var subQ1=sQuery(id+"F0.wireOp",EDGE,"E18");var subQ2=makeQuery(id+"F0.imprint","INTERSECT",VERTEX,{"derivedFrom":[subQ1,subQ0]});Q36=makeQuery(id+"F0.imprint","IMPRINT",FACE,{"disambiguationData":[TD([[makeQuery(id+"F0.imprint","IMPRINT",EDGE,{"disambiguationData":[TD([[subQ2,-1.0]])],"derivedFrom":subQ1}),1.0]])]});}
            var Q37;
            {var subQ0=sQuery(id+"F0.wireOp",EDGE,"E22.right");var subQ1=sQuery(id+"F0.wireOp",EDGE,"E22.top");var subQ2=makeQuery(id+"F0.imprint","INTERSECT",VERTEX,{"derivedFrom":[subQ1,subQ0]});Q37=makeQuery(id+"F0.imprint","IMPRINT",FACE,{"disambiguationData":[TD([[makeQuery(id+"F0.imprint","IMPRINT",EDGE,{"disambiguationData":[TD([[subQ2,1.0]])],"derivedFrom":subQ1}),-1.0]])]});}
            var Q38;
            {var subQ0=sQuery(id+"F0.wireOp",EDGE,"E22.right");var subQ1=sQuery(id+"F0.wireOp",EDGE,"E22.top");var subQ2=makeQuery(id+"F0.imprint","INTERSECT",VERTEX,{"derivedFrom":[subQ1,subQ0]});Q38=makeQuery(id+"F0.imprint","IMPRINT",FACE,{"disambiguationData":[TD([[makeQuery(id+"F0.imprint","IMPRINT",EDGE,{"disambiguationData":[TD([[subQ2,1.0]])],"derivedFrom":subQ1}),1.0]])]});}
            var Q39;
            {var subQ1=sQuery(id+"F0.wireOp",EDGE,"E11.top");var subQ3=sQuery(id+"F0.wireOp",EDGE,"E18");var subQ4=makeQuery(id+"F0.imprint","INTERSECT",VERTEX,{"derivedFrom":[subQ1,subQ3]});Q39=makeQuery(id+"F0.imprint","IMPRINT",FACE,{"disambiguationData":[TD([[makeQuery(id+"F0.imprint","IMPRINT",EDGE,{"disambiguationData":[TD([[subQ4,1.0]])],"derivedFrom":subQ3}),1.0]])]});}
            extrude(context, id + "F3", {"entities" : qUnion([Q0, Q1, Q2, Q3, Q4, Q5, Q6, Q7, Q8, Q9, Q10, Q11, Q12, Q13, Q14, Q15, Q16, Q17, Q18, Q19, Q20, Q21, Q22, Q23, Q24, Q25, Q26, Q27, Q28, Q29, Q30, Q31, Q32, Q33, Q34, Q35, Q36, Q37, Q38, Q39]), "depth" : 1.8 * mm});
        }
        {
            var Q0;
            {var subQ0=sQuery(id+"F0.wireOp",EDGE,"E10");var subQ5=sQuery(id+"F0.wireOp",EDGE,"E8");var subQ6=makeQuery(id+"F0.imprint","INTERSECT",VERTEX,{"derivedFrom":[subQ5,subQ0]});Q0=makeQuery(id+"F0.imprint","IMPRINT",FACE,{"disambiguationData":[TD([[makeQuery(id+"F0.imprint","IMPRINT",EDGE,{"disambiguationData":[TD([[subQ6,-1.0]])],"derivedFrom":subQ5}),1.0]])]});}
            var Q1;
            {var subQ5=sQuery(id+"F0.wireOp",EDGE,"E8");var subQ8=makeQuery(id+"F0.imprint","INTERSECT",VERTEX,{"derivedFrom":[subQ5,sQuery(id+"F0.wireOp",EDGE,"E12")]});Q1=makeQuery(id+"F0.imprint","IMPRINT",FACE,{"disambiguationData":[TD([[makeQuery(id+"F0.imprint","IMPRINT",EDGE,{"disambiguationData":[TD([[subQ8,1.0]])],"derivedFrom":subQ5}),1.0]])]});}
            var Q2;
            {var subQ0=sQuery(id+"F0.wireOp",EDGE,"E20");var subQ5=sQuery(id+"F0.wireOp",EDGE,"E1");var subQ9=makeQuery(id+"F0.imprint","INTERSECT",VERTEX,{"derivedFrom":[subQ5,subQ0]});Q2=makeQuery(id+"F0.imprint","IMPRINT",FACE,{"disambiguationData":[TD([[makeQuery(id+"F0.imprint","IMPRINT",EDGE,{"disambiguationData":[TD([[subQ9,-1.0]])],"derivedFrom":subQ5}),1.0]])]});}
            var Q3;
            {var subQ5=sQuery(id+"F0.wireOp",EDGE,"E1");var subQ8=makeQuery(id+"F0.imprint","INTERSECT",VERTEX,{"derivedFrom":[subQ5,sQuery(id+"F0.wireOp",EDGE,"E13")]});Q3=makeQuery(id+"F0.imprint","IMPRINT",FACE,{"disambiguationData":[TD([[makeQuery(id+"F0.imprint","IMPRINT",EDGE,{"disambiguationData":[TD([[subQ8,1.0]])],"derivedFrom":subQ5}),1.0]])]});}
            var Q4;
            {var subQ3=sQuery(id+"F0.wireOp",EDGE,"E21");var subQ5=sQuery(id+"F0.wireOp",EDGE,"E6");var subQ7=makeQuery(id+"F0.imprint","INTERSECT",VERTEX,{"derivedFrom":[subQ5,subQ3]});Q4=makeQuery(id+"F0.imprint","IMPRINT",FACE,{"disambiguationData":[TD([[makeQuery(id+"F0.imprint","IMPRINT",EDGE,{"disambiguationData":[TD([[subQ7,-1.0]])],"derivedFrom":subQ5}),1.0]])]});}
            var Q5;
            {var subQ5=sQuery(id+"F0.wireOp",EDGE,"E6");var subQ8=makeQuery(id+"F0.imprint","INTERSECT",VERTEX,{"derivedFrom":[subQ5,sQuery(id+"F0.wireOp",EDGE,"E27")]});Q5=makeQuery(id+"F0.imprint","IMPRINT",FACE,{"disambiguationData":[TD([[makeQuery(id+"F0.imprint","IMPRINT",EDGE,{"disambiguationData":[TD([[subQ8,1.0]])],"derivedFrom":subQ5}),1.0]])]});}
            extrude(context, id + "F4", {"entities" : qUnion([Q0, Q1, Q2, Q3, Q4, Q5]), "oppositeDirection" : true, "depth" : 9.6 * mm});
        }
        {
            var Q0;
            {var subQ19=sQuery(id+"F0.wireOp",EDGE,"E3.top");Q0=makeQuery(id+"F0.imprint","IMPRINT",FACE,{"disambiguationData":[TD([[makeQuery(id+"F0.imprint","IMPRINT",EDGE,{"derivedFrom":subQ19}),1.0]])]});}
            var Q1;
            {var subQ21=sQuery(id+"F0.wireOp",EDGE,"E3.bottom");Q1=makeQuery(id+"F0.imprint","IMPRINT",FACE,{"disambiguationData":[TD([[makeQuery(id+"F0.imprint","IMPRINT",EDGE,{"derivedFrom":subQ21}),-1.0]])]});}
            var Q2;
            {var subQ0=sQuery(id+"F0.wireOp",EDGE,"E14");var subQ1=sQuery(id+"F0.wireOp",EDGE,"E6");var subQ2=makeQuery(id+"F0.imprint","INTERSECT",VERTEX,{"derivedFrom":[subQ1,subQ0]});Q2=makeQuery(id+"F0.imprint","IMPRINT",FACE,{"disambiguationData":[TD([[makeQuery(id+"F0.imprint","IMPRINT",EDGE,{"disambiguationData":[TD([[subQ2,-1.0]])],"derivedFrom":subQ1}),-1.0]])]});}
            var Q3;
            {var subQ0=sQuery(id+"F0.wireOp",EDGE,"E27");var subQ1=sQuery(id+"F0.wireOp",EDGE,"E6");var subQ2=makeQuery(id+"F0.imprint","INTERSECT",VERTEX,{"derivedFrom":[subQ1,subQ0]});Q3=makeQuery(id+"F0.imprint","IMPRINT",FACE,{"disambiguationData":[TD([[makeQuery(id+"F0.imprint","IMPRINT",EDGE,{"disambiguationData":[TD([[subQ2,-1.0]])],"derivedFrom":subQ1}),-1.0]])]});}
            var Q4;
            {var subQ0=sQuery(id+"F0.wireOp",EDGE,"E13");var subQ1=sQuery(id+"F0.wireOp",EDGE,"E1");var subQ2=makeQuery(id+"F0.imprint","INTERSECT",VERTEX,{"derivedFrom":[subQ1,subQ0]});Q4=makeQuery(id+"F0.imprint","IMPRINT",FACE,{"disambiguationData":[TD([[makeQuery(id+"F0.imprint","IMPRINT",EDGE,{"disambiguationData":[TD([[subQ2,-1.0]])],"derivedFrom":subQ1}),-1.0]])]});}
            var Q5;
            {var subQ0=sQuery(id+"F0.wireOp",EDGE,"E15");var subQ1=sQuery(id+"F0.wireOp",EDGE,"E1");var subQ2=makeQuery(id+"F0.imprint","INTERSECT",VERTEX,{"derivedFrom":[subQ1,subQ0]});Q5=makeQuery(id+"F0.imprint","IMPRINT",FACE,{"disambiguationData":[TD([[makeQuery(id+"F0.imprint","IMPRINT",EDGE,{"disambiguationData":[TD([[subQ2,-1.0]])],"derivedFrom":subQ1}),-1.0]])]});}
            var Q6;
            {var subQ0=sQuery(id+"F0.wireOp",EDGE,"E25");var subQ1=sQuery(id+"F0.wireOp",EDGE,"E8");var subQ2=makeQuery(id+"F0.imprint","INTERSECT",VERTEX,{"derivedFrom":[subQ1,subQ0]});Q6=makeQuery(id+"F0.imprint","IMPRINT",FACE,{"disambiguationData":[TD([[makeQuery(id+"F0.imprint","IMPRINT",EDGE,{"disambiguationData":[TD([[subQ2,-1.0]])],"derivedFrom":subQ1}),-1.0]])]});}
            var Q7;
            {var subQ0=sQuery(id+"F0.wireOp",EDGE,"E12");var subQ1=sQuery(id+"F0.wireOp",EDGE,"E8");var subQ2=makeQuery(id+"F0.imprint","INTERSECT",VERTEX,{"derivedFrom":[subQ1,subQ0]});Q7=makeQuery(id+"F0.imprint","IMPRINT",FACE,{"disambiguationData":[TD([[makeQuery(id+"F0.imprint","IMPRINT",EDGE,{"disambiguationData":[TD([[subQ2,-1.0]])],"derivedFrom":subQ1}),-1.0]])]});}
            var Q8;
            {var subQ9=sQuery(id+"F0.wireOp",EDGE,"E34.right");var subQ11=sQuery(id+"F0.wireOp",EDGE,"E3.top");var subQ12=makeQuery(id+"F0.imprint","INTERSECT",VERTEX,{"derivedFrom":[subQ11,subQ9]});Q8=makeQuery(id+"F0.imprint","IMPRINT",FACE,{"disambiguationData":[TD([[makeQuery(id+"F0.imprint","IMPRINT",EDGE,{"disambiguationData":[TD([[subQ12,-1.0]])],"derivedFrom":subQ11}),1.0]])]});}
            var Q9;
            {var subQ3=sQuery(id+"F0.wireOp",EDGE,"E3.right");var subQ5=sQuery(id+"F0.wireOp",EDGE,"E3.top");var subQ6=makeQuery(id+"F0.imprint","INTERSECT",VERTEX,{"derivedFrom":[subQ5,subQ3]});Q9=makeQuery(id+"F0.imprint","IMPRINT",FACE,{"disambiguationData":[TD([[makeQuery(id+"F0.imprint","IMPRINT",EDGE,{"disambiguationData":[TD([[subQ6,1.0]])],"derivedFrom":subQ5}),1.0]])]});}
            var Q10;
            {var subQ0=sQuery(id+"F0.wireOp",EDGE,"E10");var subQ1=sQuery(id+"F0.wireOp",EDGE,"E3.right");var subQ2=makeQuery(id+"F0.imprint","INTERSECT",VERTEX,{"derivedFrom":[subQ1,subQ0]});Q10=makeQuery(id+"F0.imprint","IMPRINT",FACE,{"disambiguationData":[TD([[makeQuery(id+"F0.imprint","IMPRINT",EDGE,{"disambiguationData":[TD([[subQ2,-1.0]])],"derivedFrom":subQ1}),-1.0]])]});}
            var Q11;
            {var subQ1=sQuery(id+"F0.wireOp",EDGE,"E10");var subQ7=sQuery(id+"F0.wireOp",EDGE,"E3.right");var subQ8=makeQuery(id+"F0.imprint","INTERSECT",VERTEX,{"derivedFrom":[subQ7,subQ1]});Q11=makeQuery(id+"F0.imprint","IMPRINT",FACE,{"disambiguationData":[TD([[makeQuery(id+"F0.imprint","IMPRINT",EDGE,{"disambiguationData":[TD([[subQ8,1.0]])],"derivedFrom":subQ7}),-1.0]])]});}
            var Q12;
            {var subQ3=sQuery(id+"F0.wireOp",EDGE,"E3.right");var subQ9=sQuery(id+"F0.wireOp",EDGE,"E3.bottom");var subQ10=makeQuery(id+"F0.imprint","INTERSECT",VERTEX,{"derivedFrom":[subQ9,subQ3]});Q12=makeQuery(id+"F0.imprint","IMPRINT",FACE,{"disambiguationData":[TD([[makeQuery(id+"F0.imprint","IMPRINT",EDGE,{"disambiguationData":[TD([[subQ10,1.0]])],"derivedFrom":subQ9}),-1.0]])]});}
            var Q13;
            {var subQ11=sQuery(id+"F0.wireOp",EDGE,"E39.right");var subQ12=sQuery(id+"F0.wireOp",EDGE,"E3.bottom");var subQ13=makeQuery(id+"F0.imprint","INTERSECT",VERTEX,{"derivedFrom":[subQ12,subQ11]});Q13=makeQuery(id+"F0.imprint","IMPRINT",FACE,{"disambiguationData":[TD([[makeQuery(id+"F0.imprint","IMPRINT",EDGE,{"disambiguationData":[TD([[subQ13,-1.0]])],"derivedFrom":subQ12}),-1.0]])]});}
            var Q14;
            {var subQ9=sQuery(id+"F0.wireOp",EDGE,"E40.right");var subQ10=sQuery(id+"F0.wireOp",EDGE,"E3.bottom");var subQ11=makeQuery(id+"F0.imprint","INTERSECT",VERTEX,{"derivedFrom":[subQ10,subQ9]});Q14=makeQuery(id+"F0.imprint","IMPRINT",FACE,{"disambiguationData":[TD([[makeQuery(id+"F0.imprint","IMPRINT",EDGE,{"disambiguationData":[TD([[subQ11,-1.0]])],"derivedFrom":subQ10}),-1.0]])]});}
            var Q15;
            {var subQ9=sQuery(id+"F0.wireOp",EDGE,"E35.right");var subQ10=sQuery(id+"F0.wireOp",EDGE,"E3.top");var subQ11=makeQuery(id+"F0.imprint","INTERSECT",VERTEX,{"derivedFrom":[subQ10,subQ9]});Q15=makeQuery(id+"F0.imprint","IMPRINT",FACE,{"disambiguationData":[TD([[makeQuery(id+"F0.imprint","IMPRINT",EDGE,{"disambiguationData":[TD([[subQ11,-1.0]])],"derivedFrom":subQ10}),1.0]])]});}
            var Q16;
            {var subQ9=sQuery(id+"F0.wireOp",EDGE,"E36.right");var subQ10=sQuery(id+"F0.wireOp",EDGE,"E3.top");var subQ11=makeQuery(id+"F0.imprint","INTERSECT",VERTEX,{"derivedFrom":[subQ10,subQ9]});Q16=makeQuery(id+"F0.imprint","IMPRINT",FACE,{"disambiguationData":[TD([[makeQuery(id+"F0.imprint","IMPRINT",EDGE,{"disambiguationData":[TD([[subQ11,-1.0]])],"derivedFrom":subQ10}),1.0]])]});}
            var Q17;
            {var subQ8=sQuery(id+"F0.wireOp",EDGE,"E3.left");var subQ11=sQuery(id+"F0.wireOp",EDGE,"E3.top");var subQ12=makeQuery(id+"F0.imprint","INTERSECT",VERTEX,{"derivedFrom":[subQ11,subQ8]});Q17=makeQuery(id+"F0.imprint","IMPRINT",FACE,{"disambiguationData":[TD([[makeQuery(id+"F0.imprint","IMPRINT",EDGE,{"disambiguationData":[TD([[subQ12,-1.0]])],"derivedFrom":subQ11}),1.0]])]});}
            var Q18;
            {var subQ5=sQuery(id+"F0.wireOp",EDGE,"E10");var subQ7=sQuery(id+"F0.wireOp",EDGE,"E3.left");var subQ8=makeQuery(id+"F0.imprint","INTERSECT",VERTEX,{"derivedFrom":[subQ7,subQ5]});Q18=makeQuery(id+"F0.imprint","IMPRINT",FACE,{"disambiguationData":[TD([[makeQuery(id+"F0.imprint","IMPRINT",EDGE,{"disambiguationData":[TD([[subQ8,-1.0]])],"derivedFrom":subQ7}),1.0]])]});}
            var Q19;
            {var subQ5=sQuery(id+"F0.wireOp",EDGE,"E10");var subQ7=sQuery(id+"F0.wireOp",EDGE,"E3.left");var subQ8=makeQuery(id+"F0.imprint","INTERSECT",VERTEX,{"derivedFrom":[subQ7,subQ5]});Q19=makeQuery(id+"F0.imprint","IMPRINT",FACE,{"disambiguationData":[TD([[makeQuery(id+"F0.imprint","IMPRINT",EDGE,{"disambiguationData":[TD([[subQ8,1.0]])],"derivedFrom":subQ7}),1.0]])]});}
            var Q20;
            {var subQ9=sQuery(id+"F0.wireOp",EDGE,"E3.left");var subQ10=sQuery(id+"F0.wireOp",EDGE,"E3.bottom");var subQ11=makeQuery(id+"F0.imprint","INTERSECT",VERTEX,{"derivedFrom":[subQ10,subQ9]});Q20=makeQuery(id+"F0.imprint","IMPRINT",FACE,{"disambiguationData":[TD([[makeQuery(id+"F0.imprint","IMPRINT",EDGE,{"disambiguationData":[TD([[subQ11,-1.0]])],"derivedFrom":subQ10}),-1.0]])]});}
            var Q21;
            {var subQ7=sQuery(id+"F0.wireOp",EDGE,"E41.right");var subQ11=sQuery(id+"F0.wireOp",EDGE,"E3.bottom");var subQ12=makeQuery(id+"F0.imprint","INTERSECT",VERTEX,{"derivedFrom":[subQ11,subQ7]});Q21=makeQuery(id+"F0.imprint","IMPRINT",FACE,{"disambiguationData":[TD([[makeQuery(id+"F0.imprint","IMPRINT",EDGE,{"disambiguationData":[TD([[subQ12,-1.0]])],"derivedFrom":subQ11}),-1.0]])]});}
            extrude(context, id + "F5", {"entities" : qUnion([Q0, Q1, Q2, Q3, Q4, Q5, Q6, Q7, Q8, Q9, Q10, Q11, Q12, Q13, Q14, Q15, Q16, Q17, Q18, Q19, Q20, Q21]), "oppositeDirection" : true, "depth" : 1 * mm});
        }
        {
            var Q0;
            {var subQ0=sQuery(id+"F0.wireOp",EDGE,"E10");var subQ1=sQuery(id+"F0.wireOp",EDGE,"E9");var subQ2=makeQuery(id+"F0.imprint","INTERSECT",VERTEX,{"derivedFrom":[subQ1,subQ0]});Q0=makeQuery(id+"F0.imprint","IMPRINT",FACE,{"disambiguationData":[TD([[makeQuery(id+"F0.imprint","IMPRINT",EDGE,{"disambiguationData":[TD([[subQ2,1.0]])],"derivedFrom":subQ1}),1.0]])]});}
            var Q1;
            {var subQ0=sQuery(id+"F0.wireOp",EDGE,"E10");var subQ1=sQuery(id+"F0.wireOp",EDGE,"E9");var subQ2=makeQuery(id+"F0.imprint","INTERSECT",VERTEX,{"derivedFrom":[subQ1,subQ0]});Q1=makeQuery(id+"F0.imprint","IMPRINT",FACE,{"disambiguationData":[TD([[makeQuery(id+"F0.imprint","IMPRINT",EDGE,{"disambiguationData":[TD([[subQ2,-1.0]])],"derivedFrom":subQ1}),1.0]])]});}
            var Q2;
            {var subQ0=sQuery(id+"F0.wireOp",EDGE,"E20");var subQ1=sQuery(id+"F0.wireOp",EDGE,"E2");var subQ2=makeQuery(id+"F0.imprint","INTERSECT",VERTEX,{"derivedFrom":[subQ1,subQ0]});Q2=makeQuery(id+"F0.imprint","IMPRINT",FACE,{"disambiguationData":[TD([[makeQuery(id+"F0.imprint","IMPRINT",EDGE,{"disambiguationData":[TD([[subQ2,1.0]])],"derivedFrom":subQ1}),1.0]])]});}
            var Q3;
            {var subQ0=sQuery(id+"F0.wireOp",EDGE,"E20");var subQ1=sQuery(id+"F0.wireOp",EDGE,"E2");var subQ2=makeQuery(id+"F0.imprint","INTERSECT",VERTEX,{"derivedFrom":[subQ1,subQ0]});Q3=makeQuery(id+"F0.imprint","IMPRINT",FACE,{"disambiguationData":[TD([[makeQuery(id+"F0.imprint","IMPRINT",EDGE,{"disambiguationData":[TD([[subQ2,-1.0]])],"derivedFrom":subQ1}),1.0]])]});}
            var Q4;
            {var subQ0=sQuery(id+"F0.wireOp",EDGE,"E10");var subQ1=sQuery(id+"F0.wireOp",EDGE,"E7");var subQ2=makeQuery(id+"F0.imprint","INTERSECT",VERTEX,{"derivedFrom":[subQ1,subQ0]});Q4=makeQuery(id+"F0.imprint","IMPRINT",FACE,{"disambiguationData":[TD([[makeQuery(id+"F0.imprint","IMPRINT",EDGE,{"disambiguationData":[TD([[subQ2,-1.0]])],"derivedFrom":subQ1}),1.0]])]});}
            var Q5;
            {var subQ0=sQuery(id+"F0.wireOp",EDGE,"E10");var subQ1=sQuery(id+"F0.wireOp",EDGE,"E7");var subQ2=makeQuery(id+"F0.imprint","INTERSECT",VERTEX,{"derivedFrom":[subQ1,subQ0]});Q5=makeQuery(id+"F0.imprint","IMPRINT",FACE,{"disambiguationData":[TD([[makeQuery(id+"F0.imprint","IMPRINT",EDGE,{"disambiguationData":[TD([[subQ2,1.0]])],"derivedFrom":subQ1}),1.0]])]});}
            extrude(context, id + "F6", {"entities" : qUnion([Q0, Q1, Q2, Q3, Q4, Q5]), "oppositeDirection" : true, "depth" : 1 * mm});
        }
        {
            var Q0;
            {var subQ0=sQuery(id+"F0.wireOp",EDGE,"E24");var subQ1=sQuery(id+"F0.wireOp",EDGE,"E8");var subQ2=makeQuery(id+"F0.imprint","INTERSECT",VERTEX,{"derivedFrom":[subQ1,subQ0]});Q0=makeQuery(id+"F0.imprint","IMPRINT",FACE,{"disambiguationData":[TD([[makeQuery(id+"F0.imprint","IMPRINT",EDGE,{"disambiguationData":[TD([[subQ2,-1.0]])],"derivedFrom":subQ1}),-1.0]])]});}
            var Q1;
            {var subQ0=sQuery(id+"F0.wireOp",EDGE,"E10");var subQ1=sQuery(id+"F0.wireOp",EDGE,"E8");var subQ2=makeQuery(id+"F0.imprint","INTERSECT",VERTEX,{"derivedFrom":[subQ1,subQ0]});Q1=makeQuery(id+"F0.imprint","IMPRINT",FACE,{"disambiguationData":[TD([[makeQuery(id+"F0.imprint","IMPRINT",EDGE,{"disambiguationData":[TD([[subQ2,-1.0]])],"derivedFrom":subQ1}),-1.0]])]});}
            var Q2;
            {var subQ0=sQuery(id+"F0.wireOp",EDGE,"E20");var subQ1=sQuery(id+"F0.wireOp",EDGE,"E8");var subQ2=makeQuery(id+"F0.imprint","INTERSECT",VERTEX,{"derivedFrom":[subQ1,subQ0]});Q2=makeQuery(id+"F0.imprint","IMPRINT",FACE,{"disambiguationData":[TD([[makeQuery(id+"F0.imprint","IMPRINT",EDGE,{"disambiguationData":[TD([[subQ2,1.0]])],"derivedFrom":subQ1}),-1.0]])]});}
            var Q3;
            {var subQ0=sQuery(id+"F0.wireOp",EDGE,"E12");var subQ1=sQuery(id+"F0.wireOp",EDGE,"E8");var subQ2=makeQuery(id+"F0.imprint","INTERSECT",VERTEX,{"derivedFrom":[subQ1,subQ0]});Q3=makeQuery(id+"F0.imprint","IMPRINT",FACE,{"disambiguationData":[TD([[makeQuery(id+"F0.imprint","IMPRINT",EDGE,{"disambiguationData":[TD([[subQ2,1.0]])],"derivedFrom":subQ1}),-1.0]])]});}
            var Q4;
            {var subQ0=sQuery(id+"F0.wireOp",EDGE,"E12");var subQ1=sQuery(id+"F0.wireOp",EDGE,"E1");var subQ2=makeQuery(id+"F0.imprint","INTERSECT",VERTEX,{"derivedFrom":[subQ1,subQ0]});Q4=makeQuery(id+"F0.imprint","IMPRINT",FACE,{"disambiguationData":[TD([[makeQuery(id+"F0.imprint","IMPRINT",EDGE,{"disambiguationData":[TD([[subQ2,-1.0]])],"derivedFrom":subQ1}),-1.0]])]});}
            var Q5;
            {var subQ0=sQuery(id+"F0.wireOp",EDGE,"E20");var subQ1=sQuery(id+"F0.wireOp",EDGE,"E1");var subQ2=makeQuery(id+"F0.imprint","INTERSECT",VERTEX,{"derivedFrom":[subQ1,subQ0]});Q5=makeQuery(id+"F0.imprint","IMPRINT",FACE,{"disambiguationData":[TD([[makeQuery(id+"F0.imprint","IMPRINT",EDGE,{"disambiguationData":[TD([[subQ2,-1.0]])],"derivedFrom":subQ1}),-1.0]])]});}
            var Q6;
            {var subQ0=sQuery(id+"F0.wireOp",EDGE,"E13");var subQ1=sQuery(id+"F0.wireOp",EDGE,"E1");var subQ2=makeQuery(id+"F0.imprint","INTERSECT",VERTEX,{"derivedFrom":[subQ1,subQ0]});Q6=makeQuery(id+"F0.imprint","IMPRINT",FACE,{"disambiguationData":[TD([[makeQuery(id+"F0.imprint","IMPRINT",EDGE,{"disambiguationData":[TD([[subQ2,1.0]])],"derivedFrom":subQ1}),-1.0]])]});}
            var Q7;
            {var subQ0=sQuery(id+"F0.wireOp",EDGE,"E13");var subQ1=sQuery(id+"F0.wireOp",EDGE,"E6");var subQ2=makeQuery(id+"F0.imprint","INTERSECT",VERTEX,{"derivedFrom":[subQ1,subQ0]});Q7=makeQuery(id+"F0.imprint","IMPRINT",FACE,{"disambiguationData":[TD([[makeQuery(id+"F0.imprint","IMPRINT",EDGE,{"disambiguationData":[TD([[subQ2,-1.0]])],"derivedFrom":subQ1}),-1.0]])]});}
            var Q8;
            {var subQ0=sQuery(id+"F0.wireOp",EDGE,"E21");var subQ1=sQuery(id+"F0.wireOp",EDGE,"E6");var subQ2=makeQuery(id+"F0.imprint","INTERSECT",VERTEX,{"derivedFrom":[subQ1,subQ0]});Q8=makeQuery(id+"F0.imprint","IMPRINT",FACE,{"disambiguationData":[TD([[makeQuery(id+"F0.imprint","IMPRINT",EDGE,{"disambiguationData":[TD([[subQ2,-1.0]])],"derivedFrom":subQ1}),-1.0]])]});}
            var Q9;
            {var subQ0=sQuery(id+"F0.wireOp",EDGE,"E21");var subQ1=sQuery(id+"F0.wireOp",EDGE,"E1");var subQ2=makeQuery(id+"F0.imprint","INTERSECT",VERTEX,{"derivedFrom":[subQ1,subQ0]});Q9=makeQuery(id+"F0.imprint","IMPRINT",FACE,{"disambiguationData":[TD([[makeQuery(id+"F0.imprint","IMPRINT",EDGE,{"disambiguationData":[TD([[subQ2,1.0]])],"derivedFrom":subQ1}),-1.0]])]});}
            var Q10;
            {var subQ0=sQuery(id+"F0.wireOp",EDGE,"E27");var subQ1=sQuery(id+"F0.wireOp",EDGE,"E6");var subQ2=makeQuery(id+"F0.imprint","INTERSECT",VERTEX,{"derivedFrom":[subQ1,subQ0]});Q10=makeQuery(id+"F0.imprint","IMPRINT",FACE,{"disambiguationData":[TD([[makeQuery(id+"F0.imprint","IMPRINT",EDGE,{"disambiguationData":[TD([[subQ2,1.0]])],"derivedFrom":subQ1}),-1.0]])]});}
            var Q11;
            {var subQ0=sQuery(id+"F0.wireOp",EDGE,"E10");var subQ1=sQuery(id+"F0.wireOp",EDGE,"E6");var subQ2=makeQuery(id+"F0.imprint","INTERSECT",VERTEX,{"derivedFrom":[subQ1,subQ0]});Q11=makeQuery(id+"F0.imprint","IMPRINT",FACE,{"disambiguationData":[TD([[makeQuery(id+"F0.imprint","IMPRINT",EDGE,{"disambiguationData":[TD([[subQ2,1.0]])],"derivedFrom":subQ1}),-1.0]])]});}
            extrude(context, id + "F7", {"entities" : qUnion([Q0, Q1, Q2, Q3, Q4, Q5, Q6, Q7, Q8, Q9, Q10, Q11]), "oppositeDirection" : true, "depth" : 1 * mm});
        }
        {
            var Q0;
            {var subQ0=sQuery(id+"F0.wireOp",EDGE,"E25");var subQ1=sQuery(id+"F0.wireOp",EDGE,"E22.top");var subQ2=makeQuery(id+"F0.imprint","INTERSECT",VERTEX,{"derivedFrom":[subQ1,subQ0]});Q0=makeQuery(id+"F0.imprint","IMPRINT",FACE,{"disambiguationData":[TD([[makeQuery(id+"F0.imprint","IMPRINT",EDGE,{"disambiguationData":[TD([[subQ2,-1.0]])],"derivedFrom":subQ1}),1.0]])]});}
            var Q1;
            {var subQ0=sQuery(id+"F0.wireOp",EDGE,"E25");var subQ2=sQuery(id+"F0.wireOp",EDGE,"E22.top");var subQ3=makeQuery(id+"F0.imprint","INTERSECT",VERTEX,{"derivedFrom":[subQ2,subQ0]});Q1=makeQuery(id+"F0.imprint","IMPRINT",FACE,{"disambiguationData":[TD([[makeQuery(id+"F0.imprint","IMPRINT",EDGE,{"disambiguationData":[TD([[subQ3,-1.0]])],"derivedFrom":subQ2}),-1.0]])]});}
            var Q2;
            {var subQ0=sQuery(id+"F0.wireOp",EDGE,"E18");var subQ1=sQuery(id+"F0.wireOp",EDGE,"E11.top");var subQ2=makeQuery(id+"F0.imprint","INTERSECT",VERTEX,{"derivedFrom":[subQ1,subQ0]});Q2=makeQuery(id+"F0.imprint","IMPRINT",FACE,{"disambiguationData":[TD([[makeQuery(id+"F0.imprint","IMPRINT",EDGE,{"disambiguationData":[TD([[subQ2,-1.0]])],"derivedFrom":subQ1}),-1.0]])]});}
            var Q3;
            {var subQ1=sQuery(id+"F0.wireOp",EDGE,"E15");var subQ7=makeQuery(id+"F0.imprint","INTERSECT",VERTEX,{"derivedFrom":[sQuery(id+"F0.wireOp",EDGE,"E8"),subQ1]});Q3=makeQuery(id+"F0.imprint","IMPRINT",FACE,{"disambiguationData":[TD([[makeQuery(id+"F0.imprint","IMPRINT",EDGE,{"disambiguationData":[TD([[subQ7,1.0]])],"derivedFrom":subQ1}),1.0]])]});}
            var Q4;
            {var subQ0=sQuery(id+"F0.wireOp",EDGE,"E18");var subQ1=sQuery(id+"F0.wireOp",EDGE,"E11.top");var subQ2=makeQuery(id+"F0.imprint","INTERSECT",VERTEX,{"derivedFrom":[subQ1,subQ0]});Q4=makeQuery(id+"F0.imprint","IMPRINT",FACE,{"disambiguationData":[TD([[makeQuery(id+"F0.imprint","IMPRINT",EDGE,{"disambiguationData":[TD([[subQ2,-1.0]])],"derivedFrom":subQ1}),1.0]])]});}
            var Q5;
            {var subQ0=sQuery(id+"F0.wireOp",EDGE,"E14");var subQ1=sQuery(id+"F0.wireOp",EDGE,"E11.top");var subQ2=makeQuery(id+"F0.imprint","INTERSECT",VERTEX,{"derivedFrom":[subQ1,subQ0]});Q5=makeQuery(id+"F0.imprint","IMPRINT",FACE,{"disambiguationData":[TD([[makeQuery(id+"F0.imprint","IMPRINT",EDGE,{"disambiguationData":[TD([[subQ2,-1.0]])],"derivedFrom":subQ1}),-1.0]])]});}
            var Q6;
            {var subQ1=sQuery(id+"F0.wireOp",EDGE,"E11.top");var subQ5=sQuery(id+"F0.wireOp",EDGE,"E14");var subQ7=makeQuery(id+"F0.imprint","INTERSECT",VERTEX,{"derivedFrom":[subQ1,subQ5]});Q6=makeQuery(id+"F0.imprint","IMPRINT",FACE,{"disambiguationData":[TD([[makeQuery(id+"F0.imprint","IMPRINT",EDGE,{"disambiguationData":[TD([[subQ7,-1.0]])],"derivedFrom":subQ1}),1.0]])]});}
            var Q7;
            {var subQ5=sQuery(id+"F0.wireOp",EDGE,"E14");var subQ7=makeQuery(id+"F0.imprint","INTERSECT",VERTEX,{"derivedFrom":[sQuery(id+"F0.wireOp",EDGE,"E6"),subQ5]});Q7=makeQuery(id+"F0.imprint","IMPRINT",FACE,{"disambiguationData":[TD([[makeQuery(id+"F0.imprint","IMPRINT",EDGE,{"disambiguationData":[TD([[subQ7,1.0]])],"derivedFrom":subQ5}),1.0]])]});}
            var Q8;
            {var subQ0=sQuery(id+"F0.wireOp",EDGE,"E26");var subQ1=sQuery(id+"F0.wireOp",EDGE,"E23.top");var subQ2=makeQuery(id+"F0.imprint","INTERSECT",VERTEX,{"derivedFrom":[subQ1,subQ0]});Q8=makeQuery(id+"F0.imprint","IMPRINT",FACE,{"disambiguationData":[TD([[makeQuery(id+"F0.imprint","IMPRINT",EDGE,{"disambiguationData":[TD([[subQ2,-1.0]])],"derivedFrom":subQ1}),-1.0]])]});}
            var Q9;
            {var subQ0=sQuery(id+"F0.wireOp",EDGE,"E26");var subQ2=sQuery(id+"F0.wireOp",EDGE,"E23.top");var subQ3=makeQuery(id+"F0.imprint","INTERSECT",VERTEX,{"derivedFrom":[subQ2,subQ0]});Q9=makeQuery(id+"F0.imprint","IMPRINT",FACE,{"disambiguationData":[TD([[makeQuery(id+"F0.imprint","IMPRINT",EDGE,{"disambiguationData":[TD([[subQ3,-1.0]])],"derivedFrom":subQ2}),1.0]])]});}
            var Q10;
            {var subQ0=sQuery(id+"F0.wireOp",EDGE,"E27");var subQ4=sQuery(id+"F0.wireOp",EDGE,"E23.bottom");var subQ5=makeQuery(id+"F0.imprint","INTERSECT",VERTEX,{"derivedFrom":[subQ4,subQ0]});Q10=makeQuery(id+"F0.imprint","IMPRINT",FACE,{"disambiguationData":[TD([[makeQuery(id+"F0.imprint","IMPRINT",EDGE,{"disambiguationData":[TD([[subQ5,-1.0]])],"derivedFrom":subQ4}),-1.0]])]});}
            var Q11;
            {var subQ0=sQuery(id+"F0.wireOp",EDGE,"E27");var subQ1=sQuery(id+"F0.wireOp",EDGE,"E23.bottom");var subQ2=makeQuery(id+"F0.imprint","INTERSECT",VERTEX,{"derivedFrom":[subQ1,subQ0]});Q11=makeQuery(id+"F0.imprint","IMPRINT",FACE,{"disambiguationData":[TD([[makeQuery(id+"F0.imprint","IMPRINT",EDGE,{"disambiguationData":[TD([[subQ2,-1.0]])],"derivedFrom":subQ1}),1.0]])]});}
            var Q12;
            {var subQ1=sQuery(id+"F0.wireOp",EDGE,"E13");var subQ5=makeQuery(id+"F0.imprint","INTERSECT",VERTEX,{"derivedFrom":[sQuery(id+"F0.wireOp",EDGE,"E6"),subQ1]});Q12=makeQuery(id+"F0.imprint","IMPRINT",FACE,{"disambiguationData":[TD([[makeQuery(id+"F0.imprint","IMPRINT",EDGE,{"disambiguationData":[TD([[subQ5,1.0]])],"derivedFrom":subQ1}),1.0]])]});}
            var Q13;
            {var subQ1=sQuery(id+"F0.wireOp",EDGE,"E11.bottom");var subQ5=sQuery(id+"F0.wireOp",EDGE,"E13");var subQ7=makeQuery(id+"F0.imprint","INTERSECT",VERTEX,{"derivedFrom":[subQ1,subQ5]});Q13=makeQuery(id+"F0.imprint","IMPRINT",FACE,{"disambiguationData":[TD([[makeQuery(id+"F0.imprint","IMPRINT",EDGE,{"disambiguationData":[TD([[subQ7,-1.0]])],"derivedFrom":subQ1}),-1.0]])]});}
            var Q14;
            {var subQ0=sQuery(id+"F0.wireOp",EDGE,"E13");var subQ1=sQuery(id+"F0.wireOp",EDGE,"E11.bottom");var subQ2=makeQuery(id+"F0.imprint","INTERSECT",VERTEX,{"derivedFrom":[subQ1,subQ0]});Q14=makeQuery(id+"F0.imprint","IMPRINT",FACE,{"disambiguationData":[TD([[makeQuery(id+"F0.imprint","IMPRINT",EDGE,{"disambiguationData":[TD([[subQ2,-1.0]])],"derivedFrom":subQ1}),1.0]])]});}
            var Q15;
            {var subQ2=sQuery(id+"F0.wireOp",EDGE,"E11.bottom");var subQ6=sQuery(id+"F0.wireOp",EDGE,"E16");var subQ7=makeQuery(id+"F0.imprint","INTERSECT",VERTEX,{"derivedFrom":[subQ2,subQ6]});Q15=makeQuery(id+"F0.imprint","IMPRINT",FACE,{"disambiguationData":[TD([[makeQuery(id+"F0.imprint","IMPRINT",EDGE,{"disambiguationData":[TD([[subQ7,-1.0]])],"derivedFrom":subQ2}),-1.0]])]});}
            var Q16;
            {var subQ1=sQuery(id+"F0.wireOp",EDGE,"E12");var subQ7=makeQuery(id+"F0.imprint","INTERSECT",VERTEX,{"derivedFrom":[sQuery(id+"F0.wireOp",EDGE,"E8"),subQ1]});Q16=makeQuery(id+"F0.imprint","IMPRINT",FACE,{"disambiguationData":[TD([[makeQuery(id+"F0.imprint","IMPRINT",EDGE,{"disambiguationData":[TD([[subQ7,1.0]])],"derivedFrom":subQ1}),1.0]])]});}
            var Q17;
            {var subQ0=sQuery(id+"F0.wireOp",EDGE,"E16");var subQ1=sQuery(id+"F0.wireOp",EDGE,"E11.bottom");var subQ2=makeQuery(id+"F0.imprint","INTERSECT",VERTEX,{"derivedFrom":[subQ1,subQ0]});Q17=makeQuery(id+"F0.imprint","IMPRINT",FACE,{"disambiguationData":[TD([[makeQuery(id+"F0.imprint","IMPRINT",EDGE,{"disambiguationData":[TD([[subQ2,-1.0]])],"derivedFrom":subQ1}),1.0]])]});}
            var Q18;
            {var subQ0=sQuery(id+"F0.wireOp",EDGE,"E24");var subQ2=sQuery(id+"F0.wireOp",EDGE,"E22.bottom");var subQ3=makeQuery(id+"F0.imprint","INTERSECT",VERTEX,{"derivedFrom":[subQ2,subQ0]});Q18=makeQuery(id+"F0.imprint","IMPRINT",FACE,{"disambiguationData":[TD([[makeQuery(id+"F0.imprint","IMPRINT",EDGE,{"disambiguationData":[TD([[subQ3,-1.0]])],"derivedFrom":subQ2}),1.0]])]});}
            var Q19;
            {var subQ0=sQuery(id+"F0.wireOp",EDGE,"E24");var subQ1=sQuery(id+"F0.wireOp",EDGE,"E22.bottom");var subQ2=makeQuery(id+"F0.imprint","INTERSECT",VERTEX,{"derivedFrom":[subQ1,subQ0]});Q19=makeQuery(id+"F0.imprint","IMPRINT",FACE,{"disambiguationData":[TD([[makeQuery(id+"F0.imprint","IMPRINT",EDGE,{"disambiguationData":[TD([[subQ2,-1.0]])],"derivedFrom":subQ1}),-1.0]])]});}
            extrude(context, id + "F8", {"entities" : qUnion([Q0, Q1, Q2, Q3, Q4, Q5, Q6, Q7, Q8, Q9, Q10, Q11, Q12, Q13, Q14, Q15, Q16, Q17, Q18, Q19]), "oppositeDirection" : true, "depth" : 1 * mm});
        }
        {
            var Q0;
            {var subQ5=sQuery(id+"F0.wireOp",EDGE,"E34.left");var subQ8=sQuery(id+"F0.wireOp",EDGE,"E3.top");var subQ9=makeQuery(id+"F0.imprint","INTERSECT",VERTEX,{"derivedFrom":[subQ8,subQ5]});Q0=makeQuery(id+"F0.imprint","IMPRINT",FACE,{"disambiguationData":[TD([[makeQuery(id+"F0.imprint","IMPRINT",EDGE,{"disambiguationData":[TD([[subQ9,-1.0]])],"derivedFrom":subQ8}),1.0]])]});}
            var Q1;
            {var subQ5=sQuery(id+"F0.wireOp",EDGE,"E34.top");Q1=makeQuery(id+"F0.imprint","IMPRINT",FACE,{"disambiguationData":[TD([[makeQuery(id+"F0.imprint","IMPRINT",EDGE,{"derivedFrom":subQ5}),1.0]])]});}
            var Q2;
            {var subQ5=sQuery(id+"F0.wireOp",EDGE,"E35.top");Q2=makeQuery(id+"F0.imprint","IMPRINT",FACE,{"disambiguationData":[TD([[makeQuery(id+"F0.imprint","IMPRINT",EDGE,{"derivedFrom":subQ5}),1.0]])]});}
            var Q3;
            {var subQ6=sQuery(id+"F0.wireOp",EDGE,"E35.left");var subQ8=sQuery(id+"F0.wireOp",EDGE,"E3.top");var subQ9=makeQuery(id+"F0.imprint","INTERSECT",VERTEX,{"derivedFrom":[subQ8,subQ6]});Q3=makeQuery(id+"F0.imprint","IMPRINT",FACE,{"disambiguationData":[TD([[makeQuery(id+"F0.imprint","IMPRINT",EDGE,{"disambiguationData":[TD([[subQ9,-1.0]])],"derivedFrom":subQ8}),1.0]])]});}
            var Q4;
            {var subQ5=sQuery(id+"F0.wireOp",EDGE,"E36.top");Q4=makeQuery(id+"F0.imprint","IMPRINT",FACE,{"disambiguationData":[TD([[makeQuery(id+"F0.imprint","IMPRINT",EDGE,{"derivedFrom":subQ5}),1.0]])]});}
            var Q5;
            {var subQ5=sQuery(id+"F0.wireOp",EDGE,"E36.left");var subQ8=sQuery(id+"F0.wireOp",EDGE,"E3.top");var subQ9=makeQuery(id+"F0.imprint","INTERSECT",VERTEX,{"derivedFrom":[subQ8,subQ5]});Q5=makeQuery(id+"F0.imprint","IMPRINT",FACE,{"disambiguationData":[TD([[makeQuery(id+"F0.imprint","IMPRINT",EDGE,{"disambiguationData":[TD([[subQ9,-1.0]])],"derivedFrom":subQ8}),1.0]])]});}
            var Q6;
            {var subQ1=sQuery(id+"F0.wireOp",EDGE,"E43.top");var subQ3=sQuery(id+"F0.wireOp",EDGE,"E3.left");var subQ4=makeQuery(id+"F0.imprint","INTERSECT",VERTEX,{"derivedFrom":[subQ3,subQ1]});Q6=makeQuery(id+"F0.imprint","IMPRINT",FACE,{"disambiguationData":[TD([[makeQuery(id+"F0.imprint","IMPRINT",EDGE,{"disambiguationData":[TD([[subQ4,-1.0]])],"derivedFrom":subQ3}),1.0]])]});}
            var Q7;
            {var subQ5=sQuery(id+"F0.wireOp",EDGE,"E43.right");Q7=makeQuery(id+"F0.imprint","IMPRINT",FACE,{"disambiguationData":[TD([[makeQuery(id+"F0.imprint","IMPRINT",EDGE,{"derivedFrom":subQ5}),-1.0]])]});}
            var Q8;
            {var subQ1=sQuery(id+"F0.wireOp",EDGE,"E42.top");var subQ3=sQuery(id+"F0.wireOp",EDGE,"E3.left");var subQ4=makeQuery(id+"F0.imprint","INTERSECT",VERTEX,{"derivedFrom":[subQ3,subQ1]});Q8=makeQuery(id+"F0.imprint","IMPRINT",FACE,{"disambiguationData":[TD([[makeQuery(id+"F0.imprint","IMPRINT",EDGE,{"disambiguationData":[TD([[subQ4,-1.0]])],"derivedFrom":subQ3}),1.0]])]});}
            var Q9;
            {var subQ5=sQuery(id+"F0.wireOp",EDGE,"E42.right");Q9=makeQuery(id+"F0.imprint","IMPRINT",FACE,{"disambiguationData":[TD([[makeQuery(id+"F0.imprint","IMPRINT",EDGE,{"derivedFrom":subQ5}),-1.0]])]});}
            var Q10;
            {var subQ5=sQuery(id+"F0.wireOp",EDGE,"E41.top");Q10=makeQuery(id+"F0.imprint","IMPRINT",FACE,{"disambiguationData":[TD([[makeQuery(id+"F0.imprint","IMPRINT",EDGE,{"derivedFrom":subQ5}),-1.0]])]});}
            var Q11;
            {var subQ5=sQuery(id+"F0.wireOp",EDGE,"E41.left");var subQ8=sQuery(id+"F0.wireOp",EDGE,"E3.bottom");var subQ9=makeQuery(id+"F0.imprint","INTERSECT",VERTEX,{"derivedFrom":[subQ8,subQ5]});Q11=makeQuery(id+"F0.imprint","IMPRINT",FACE,{"disambiguationData":[TD([[makeQuery(id+"F0.imprint","IMPRINT",EDGE,{"disambiguationData":[TD([[subQ9,-1.0]])],"derivedFrom":subQ8}),-1.0]])]});}
            var Q12;
            {var subQ6=sQuery(id+"F0.wireOp",EDGE,"E40.left");var subQ7=sQuery(id+"F0.wireOp",EDGE,"E3.bottom");var subQ8=makeQuery(id+"F0.imprint","INTERSECT",VERTEX,{"derivedFrom":[subQ7,subQ6]});Q12=makeQuery(id+"F0.imprint","IMPRINT",FACE,{"disambiguationData":[TD([[makeQuery(id+"F0.imprint","IMPRINT",EDGE,{"disambiguationData":[TD([[subQ8,-1.0]])],"derivedFrom":subQ7}),-1.0]])]});}
            var Q13;
            {var subQ5=sQuery(id+"F0.wireOp",EDGE,"E40.top");Q13=makeQuery(id+"F0.imprint","IMPRINT",FACE,{"disambiguationData":[TD([[makeQuery(id+"F0.imprint","IMPRINT",EDGE,{"derivedFrom":subQ5}),-1.0]])]});}
            var Q14;
            {var subQ5=sQuery(id+"F0.wireOp",EDGE,"E39.left");var subQ8=sQuery(id+"F0.wireOp",EDGE,"E3.bottom");var subQ9=makeQuery(id+"F0.imprint","INTERSECT",VERTEX,{"derivedFrom":[subQ8,subQ5]});Q14=makeQuery(id+"F0.imprint","IMPRINT",FACE,{"disambiguationData":[TD([[makeQuery(id+"F0.imprint","IMPRINT",EDGE,{"disambiguationData":[TD([[subQ9,-1.0]])],"derivedFrom":subQ8}),-1.0]])]});}
            var Q15;
            {var subQ5=sQuery(id+"F0.wireOp",EDGE,"E39.top");Q15=makeQuery(id+"F0.imprint","IMPRINT",FACE,{"disambiguationData":[TD([[makeQuery(id+"F0.imprint","IMPRINT",EDGE,{"derivedFrom":subQ5}),-1.0]])]});}
            var Q16;
            {var subQ5=sQuery(id+"F0.wireOp",EDGE,"E38.top");Q16=makeQuery(id+"F0.imprint","IMPRINT",FACE,{"disambiguationData":[TD([[makeQuery(id+"F0.imprint","IMPRINT",EDGE,{"derivedFrom":subQ5}),-1.0]])]});}
            var Q17;
            {var subQ5=sQuery(id+"F0.wireOp",EDGE,"E38.left");var subQ8=sQuery(id+"F0.wireOp",EDGE,"E3.bottom");var subQ9=makeQuery(id+"F0.imprint","INTERSECT",VERTEX,{"derivedFrom":[subQ8,subQ5]});Q17=makeQuery(id+"F0.imprint","IMPRINT",FACE,{"disambiguationData":[TD([[makeQuery(id+"F0.imprint","IMPRINT",EDGE,{"disambiguationData":[TD([[subQ9,-1.0]])],"derivedFrom":subQ8}),-1.0]])]});}
            var Q18;
            {var subQ5=sQuery(id+"F0.wireOp",EDGE,"E33.right");Q18=makeQuery(id+"F0.imprint","IMPRINT",FACE,{"disambiguationData":[TD([[makeQuery(id+"F0.imprint","IMPRINT",EDGE,{"derivedFrom":subQ5}),1.0]])]});}
            var Q19;
            {var subQ1=sQuery(id+"F0.wireOp",EDGE,"E33.top");var subQ3=sQuery(id+"F0.wireOp",EDGE,"E3.right");var subQ4=makeQuery(id+"F0.imprint","INTERSECT",VERTEX,{"derivedFrom":[subQ3,subQ1]});Q19=makeQuery(id+"F0.imprint","IMPRINT",FACE,{"disambiguationData":[TD([[makeQuery(id+"F0.imprint","IMPRINT",EDGE,{"disambiguationData":[TD([[subQ4,-1.0]])],"derivedFrom":subQ3}),-1.0]])]});}
            var Q20;
            {var subQ5=sQuery(id+"F0.wireOp",EDGE,"E37.left");var subQ8=sQuery(id+"F0.wireOp",EDGE,"E3.top");var subQ9=makeQuery(id+"F0.imprint","INTERSECT",VERTEX,{"derivedFrom":[subQ8,subQ5]});Q20=makeQuery(id+"F0.imprint","IMPRINT",FACE,{"disambiguationData":[TD([[makeQuery(id+"F0.imprint","IMPRINT",EDGE,{"disambiguationData":[TD([[subQ9,-1.0]])],"derivedFrom":subQ8}),1.0]])]});}
            var Q21;
            {var subQ5=sQuery(id+"F0.wireOp",EDGE,"E37.top");Q21=makeQuery(id+"F0.imprint","IMPRINT",FACE,{"disambiguationData":[TD([[makeQuery(id+"F0.imprint","IMPRINT",EDGE,{"derivedFrom":subQ5}),1.0]])]});}
            var Q22;
            {var subQ1=sQuery(id+"F0.wireOp",EDGE,"E32.top");var subQ3=sQuery(id+"F0.wireOp",EDGE,"E3.right");var subQ4=makeQuery(id+"F0.imprint","INTERSECT",VERTEX,{"derivedFrom":[subQ3,subQ1]});Q22=makeQuery(id+"F0.imprint","IMPRINT",FACE,{"disambiguationData":[TD([[makeQuery(id+"F0.imprint","IMPRINT",EDGE,{"disambiguationData":[TD([[subQ4,-1.0]])],"derivedFrom":subQ3}),-1.0]])]});}
            var Q23;
            {var subQ5=sQuery(id+"F0.wireOp",EDGE,"E32.right");Q23=makeQuery(id+"F0.imprint","IMPRINT",FACE,{"disambiguationData":[TD([[makeQuery(id+"F0.imprint","IMPRINT",EDGE,{"derivedFrom":subQ5}),1.0]])]});}
            extrude(context, id + "F9", {"entities" : qUnion([Q0, Q1, Q2, Q3, Q4, Q5, Q6, Q7, Q8, Q9, Q10, Q11, Q12, Q13, Q14, Q15, Q16, Q17, Q18, Q19, Q20, Q21, Q22, Q23]), "oppositeDirection" : true, "depth" : 9.6 * mm});
        }
    });
